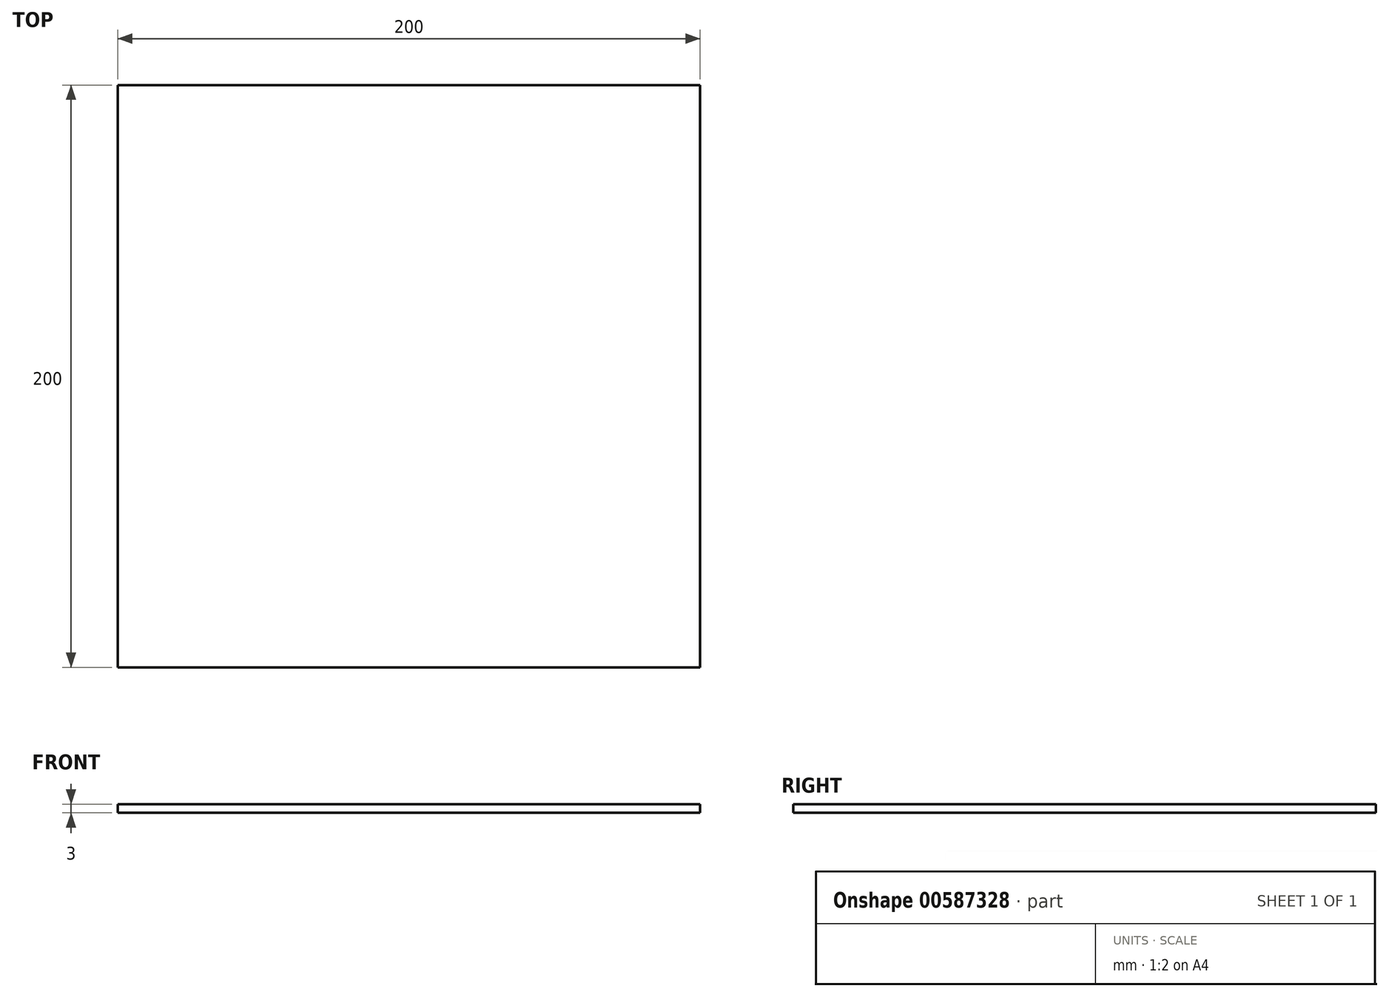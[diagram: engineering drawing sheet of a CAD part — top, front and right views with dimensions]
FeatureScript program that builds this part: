
annotation { "Feature Type Name" : "Feature", "Feature Type Description" : "" }
export const myFeature = defineFeature(function(context is Context, id is Id, definition is map)
    precondition{}
    {
        {
            var Q0;
            Q0=qCreatedBy(makeId("Top.planeOp"),FACE);
            var sketch = newSketch(context, id + "F0", { "sketchPlane" : qUnion([Q0])});
            skLineSegment(sketch, "E0.bottom", {"start": v(-100, 100) * mm, "end": v(100, 100) * mm});
            skLineSegment(sketch, "E0.top", {"start": v(-100, -100) * mm, "end": v(100, -100) * mm});
            skLineSegment(sketch, "E0.left", {"start": v(-100, 100) * mm, "end": v(-100, -100) * mm});
            skLineSegment(sketch, "E0.right", {"start": v(100, 100) * mm, "end": v(100, -100) * mm});
            skPoint(sketch, "E1", {"position": v(0, 100) * mm});
            skPoint(sketch, "E2", {"position": v(-100, 0) * mm});
            skSolve(sketch);
        }
        {
            var Q0;
            Q0 = qSketchRegion(id + "F0", true);
            extrude(context, id + "F1", {"entities" : qUnion([Q0]), "depth" : 3 * mm, "offsetDistance" : 25 * mm});
        }
    });
